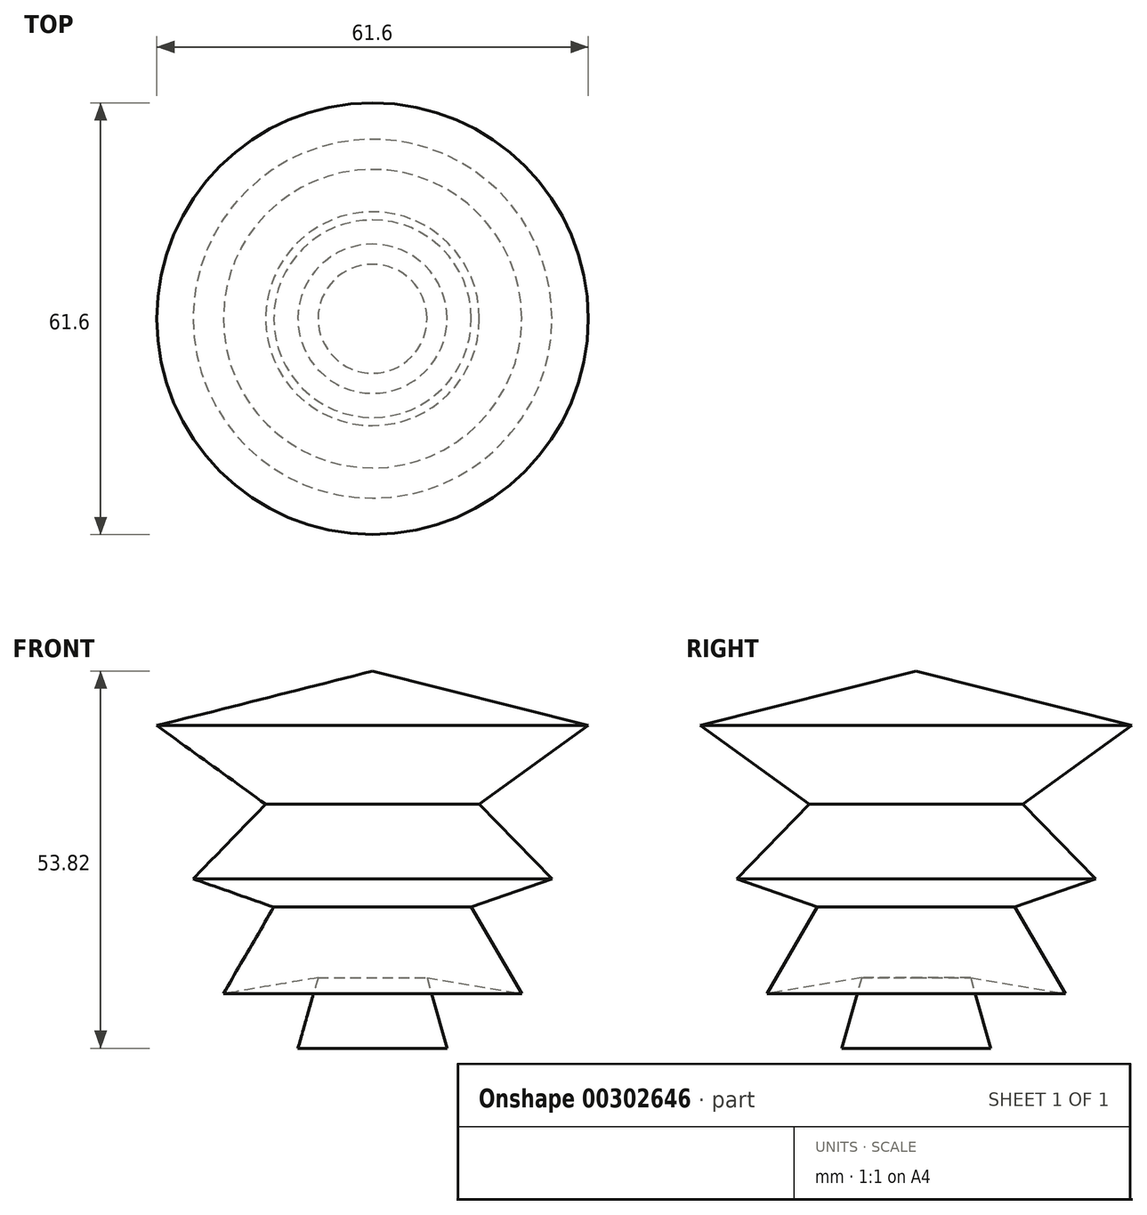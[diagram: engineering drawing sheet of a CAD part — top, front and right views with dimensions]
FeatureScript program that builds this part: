
annotation { "Feature Type Name" : "Feature", "Feature Type Description" : "" }
export const myFeature = defineFeature(function(context is Context, id is Id, definition is map)
    precondition{}
    {
        {
            var Q0;
            Q0=qCreatedBy(makeId("Front.planeOp"),FACE);
            var sketch = newSketch(context, id + "F0", { "sketchPlane" : qUnion([Q0])});
            skLineSegment(sketch, "E0", {"start": v(0, 0) * mm, "end": v(0, 53.82) * mm});
            skLineSegment(sketch, "E1", {"start": v(0, 53.82) * mm, "end": v(30.8, 46.05) * mm});
            skLineSegment(sketch, "E2", {"start": v(30.8, 46.05) * mm, "end": v(15.25, 34.82) * mm});
            skLineSegment(sketch, "E3", {"start": v(15.25, 34.82) * mm, "end": v(25.61, 24.18) * mm});
            skLineSegment(sketch, "E4", {"start": v(25.61, 24.18) * mm, "end": v(14.1, 20.15) * mm});
            skLineSegment(sketch, "E5", {"start": v(14.1, 20.15) * mm, "end": v(21.3, 7.77) * mm});
            skLineSegment(sketch, "E6", {"start": v(21.3, 7.77) * mm, "end": v(7.77, 10.07) * mm});
            skLineSegment(sketch, "E7", {"start": v(7.77, 10.07) * mm, "end": v(10.65, 0) * mm});
            skLineSegment(sketch, "E8", {"start": v(10.65, 0) * mm, "end": v(0, 0) * mm});
            skSolve(sketch);
        }
        {
            var Q0;
            Q0 = qSketchRegion(id + "F0", true);
            var Q1;
            Q1=sQuery(id+"F0.wireOp",EDGE,"E0");
            revolve(context, id + "F1", {"entities" : qUnion([Q0]), "axis" : qUnion([Q1]), "revolveType" : RevolveType.FULL});
        }
    });
